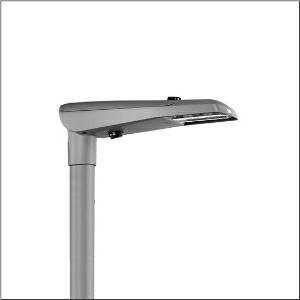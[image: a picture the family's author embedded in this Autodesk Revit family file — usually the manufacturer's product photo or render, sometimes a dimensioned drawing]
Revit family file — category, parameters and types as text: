
# Revit family: streetlight_sl_11_iq_micro___st1_2a_5xc1ac1y08ce_2333
name_source: partatom
category: Lighting Fixtures
units: mm (PartAtom-declared; Revit-internal decimal feet)

## family parameters
Cut with Voids When Loaded = No
Host = Face
Light Source = No
Part Type = Normal
Room Calculation Point = No
Round Connector Dimension = Use Diameter
Shared = No

## types (1)
- --- (1 x LED, 1600 lm, 14 W, 2200K)
    Apparent Load = 14 VA
    CIE Flux Codes = 33 71 96 100 100
    Color Rendering = 70
    Color Temperature = 2200K
    Default Elevation = 1800 mm
    Description = Streetlight SL 11 iQ micro, mast luminaire, primary light control with 3 zone facetted reflector, of plastic, silver coated, highly specular, primary optical cover: cover, of PMMA, transparent, light distribution: ST1.2a, light emission: direct distribution, primary light characteristic: asymmetric, installation type: post-top, side-entry, LED, High Power LED, rated luminous flux: 1.880lm, luminous efficacy: 136lm/W, light colour: 722/727/730/740, colour temperature: 2200/2700/3000/4000K, control gear: iQ-Street Remote, D4i with power reduction, control: pre-setting: logarithmic dimming characteristic, Street-Remote, Auto-Match, Temp-Guard, Lumen-Switch, Night-Set, Smart-Wire, Light-Fading, Desk-Remote (wireless, voltage-free reading and setting of iQ features in the workshop via application-optimized NFC function/RFID function), optimised constant luminous flux control (CLO 2.0), with cable H07RN-F 5x 1.5mm², mains connection: 220..240V, AC, 50/60Hz, connection cable pre-assembled, cable length: 5,5m, start of lifetime: 14W, end of service life: 14W, reduction: 8W, luminaire housing, of diecast aluminium, powder-coated, Siteco® metallic grey (DB 702S), please order mast flange separately, inclination adjustable without tools: 0°, 5°, 10°, 15° (post-top) | 0°, -5°, -10°, -15° (side-entry), sealing non-destructively replaceable, multi-level sealing system, length: 600mm, width: 174mm, height: 116mm, mast flange for spigot size: 42mm (side-entry): 5XC10008XM4, 60/48mm (side-entry/post-top): 5XC10108XM2, 76/60mm (side-entry/post-top): 5XC10108XM1, mounting height: 4..8m, equipment: standard, Smart Interface below and above, protection rating (complete): IP66, insulation class (complete): insulation class II (safety insulation), certification: CE, ENEC, VDE, UKCA, impact resistance: IK09, permissible operating ambient temperature for outdoor applications: -25..+50°C, standard-compliant lighting for roads and squares, Environmental Product Declaration (EPD) tested and certified by an independent institute, packaging unit: 1 piece

Light Distribution: ST1.2a
    Height = 116 mm
    Lamp = 1 x LED
    Lamp Light Flux = 1600 lm
    Lamp Power = 14 W
    Lamp count = 1
    Length = 600 mm
    Luminous efficacy = 114 lm/W
    Manufacturer = Siteco
    ModVariant = No
    Model = 5XC1AC1Y08CE
    Number of Poles = 1
    OnlyDefault = Yes
    Power Factor = 1
    Product Name = Streetlight SL 11 iQ micro | ST1.2a
    Product group = mast luminaire | pylon top
    ProductGroupID = 6100
    Protection Class = Protection class II
    Protection Degree = IP 66
    RLX_Detail_Level = 1
    RLX_Emergency_Light_Flux = 0 lm
    RLX_Emergency_Type = 0
    RLX_Emergency_Type_DB = No
    RlxData = <blob elided: 59101 chars, md5=6533831e>
    Socket = socket
    Standby Power = 0 W
    System Light Flux = 1600 lm
    System Power = 14 W
    Type Comments = individual setting: luminous flux: 100 % | dim-lin: 254 | 369 mA
    Type Image = l_1005956.jpg
    URL = http://relux.com
    VarID = @adj_031948
    Voltage = 0 V
    Weight = 0.00 kg
    Width = 174 mm

## geometry (parser evidence)
native form markers: Blend x4, Sweep x10
no freeform markers — native parametric forms only
